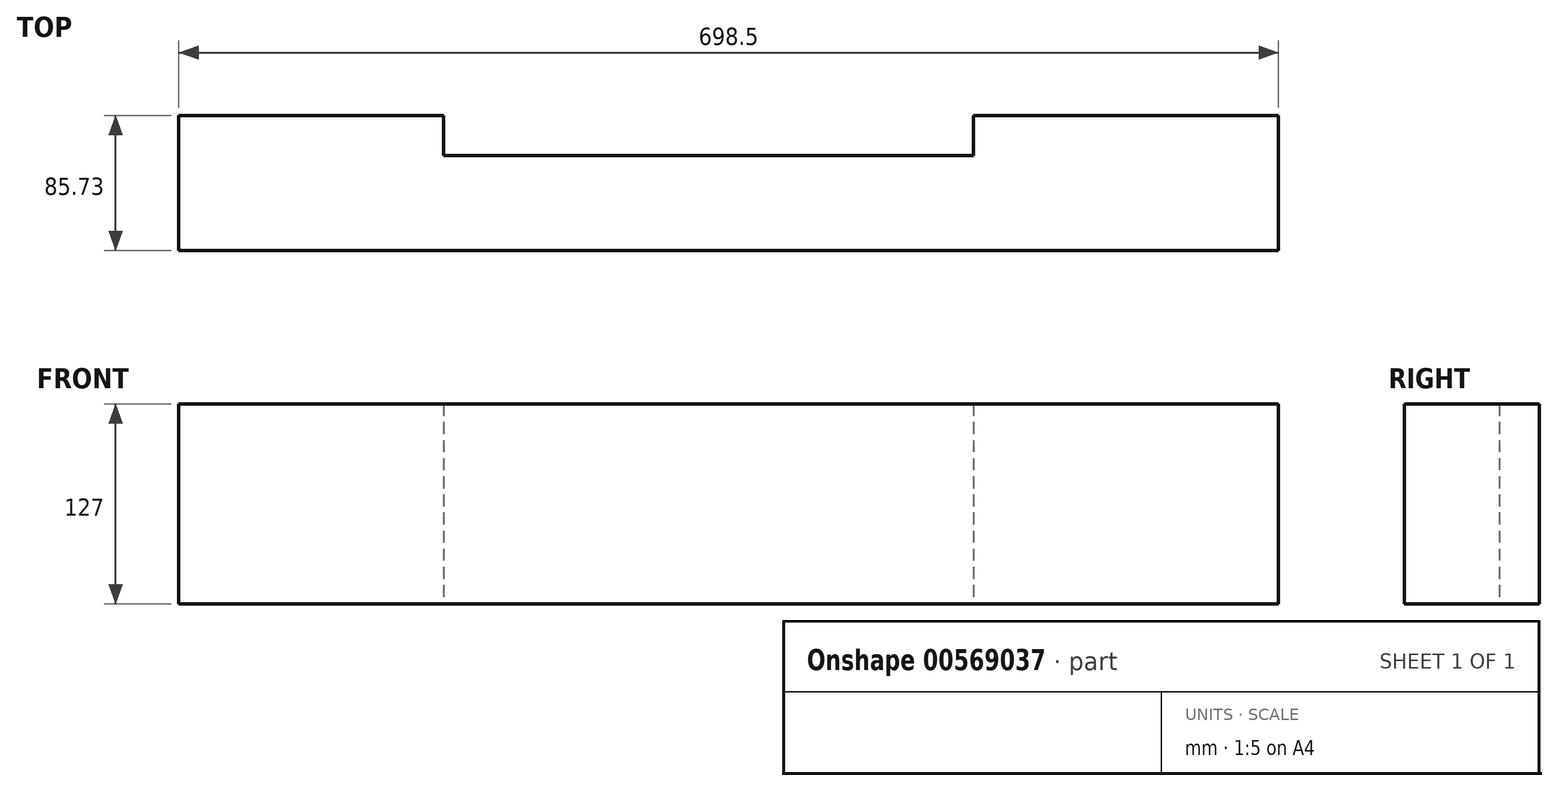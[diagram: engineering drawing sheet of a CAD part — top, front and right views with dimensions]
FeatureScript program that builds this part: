
annotation { "Feature Type Name" : "Feature", "Feature Type Description" : "" }
export const myFeature = defineFeature(function(context is Context, id is Id, definition is map)
    precondition{}
    {
        {
            var Q0;
            Q0=qCreatedBy(makeId("Top.planeOp"),FACE);
            var sketch = newSketch(context, id + "F0", { "sketchPlane" : qUnion([Q0])});
            skLineSegment(sketch, "E0.bottom", {"start": v(-349.25, -254) * mm, "end": v(349.25, -254) * mm});
            skLineSegment(sketch, "E0.top", {"start": v(-349.25, -339.72) * mm, "end": v(349.25, -339.72) * mm});
            skLineSegment(sketch, "E0.left", {"start": v(-349.25, -254) * mm, "end": v(-349.25, -339.72) * mm});
            skLineSegment(sketch, "E0.right", {"start": v(349.25, -254) * mm, "end": v(349.25, -339.72) * mm});
            skSolve(sketch);
        }
        {
            var Q0;
            Q0=makeQuery(id+"F0.imprint","IMPRINT",FACE,{"disambiguationData":[TD([[makeQuery(id+"F0.imprint","IMPRINT",EDGE,{"derivedFrom":sQuery(id+"F0.wireOp",EDGE,"E0.bottom")}),-1.0]])]});
            var sketch = newSketch(context, id + "F1", { "sketchPlane" : qUnion([Q0])});
            skLineSegment(sketch, "E1.bottom", {"start": v(-180.98, -254) * mm, "end": v(155.58, -254) * mm});
            skLineSegment(sketch, "E1.top", {"start": v(-180.98, -279.4) * mm, "end": v(155.58, -279.4) * mm});
            skLineSegment(sketch, "E1.left", {"start": v(-180.98, -254) * mm, "end": v(-180.98, -279.4) * mm});
            skLineSegment(sketch, "E1.right", {"start": v(155.58, -254) * mm, "end": v(155.58, -279.4) * mm});
            skSolve(sketch);
        }
        {
            var Q0;
            Q0=makeQuery(id+"F0.imprint","IMPRINT",FACE,{"disambiguationData":[TD([[makeQuery(id+"F0.imprint","IMPRINT",EDGE,{"derivedFrom":sQuery(id+"F0.wireOp",EDGE,"E0.bottom")}),-1.0]])]});
            extrude(context, id + "F2", {"entities" : qUnion([Q0]), "depth" : 127 * mm, "offsetDistance" : 25.4 * mm});
        }
        {
            var Q0;
            Q0 = qSketchRegion(id + "F1", true);
            extrude(context, id + "F3", {"entities" : qUnion([Q0]), "operationType" : NewBodyOperationType.REMOVE, "depth" : 127 * mm, "offsetDistance" : 25.4 * mm});
        }
    });
